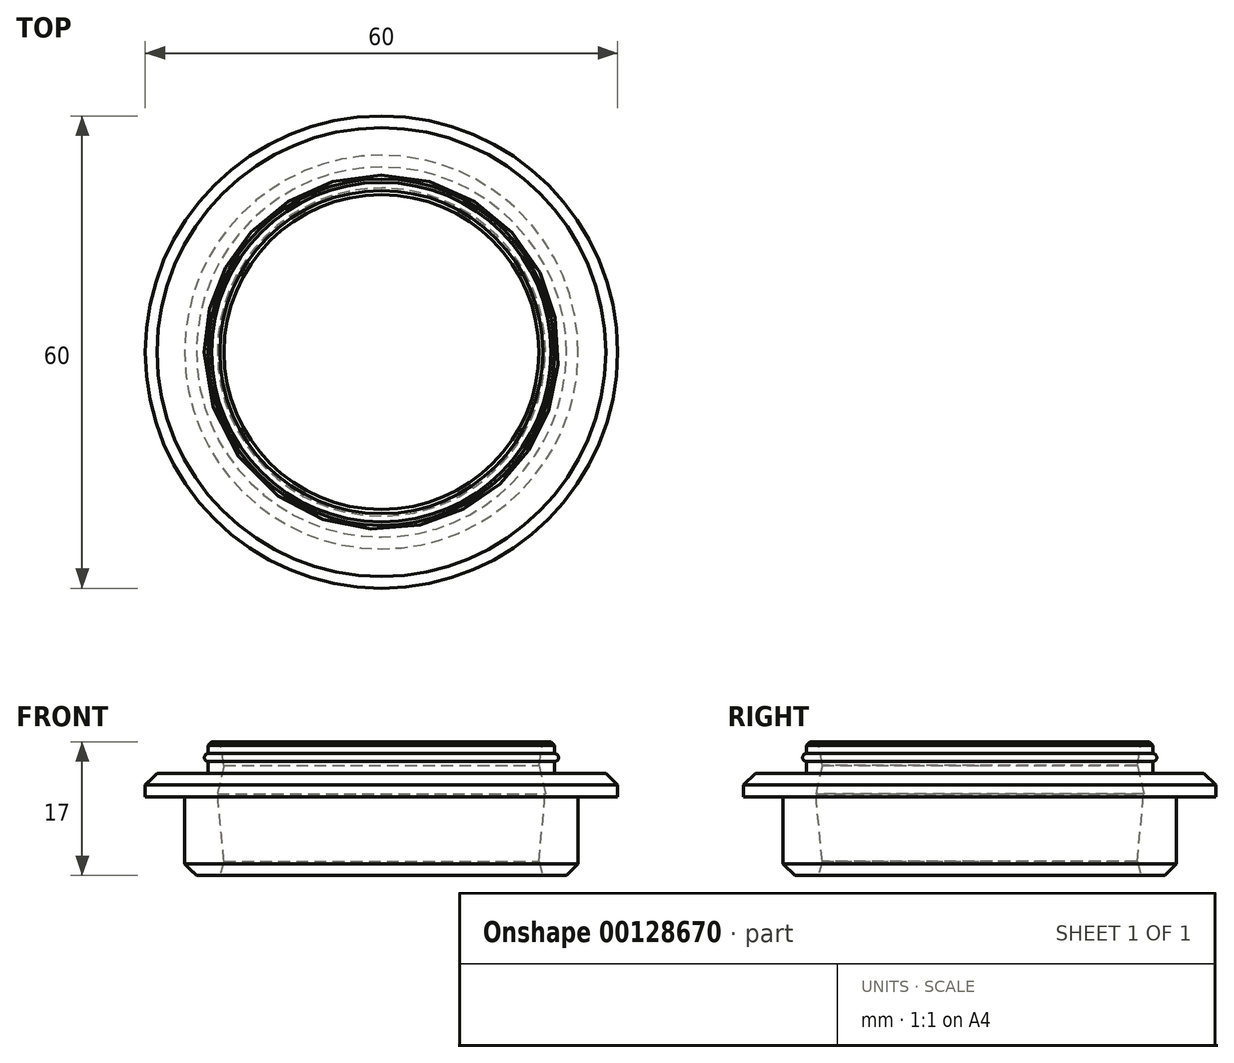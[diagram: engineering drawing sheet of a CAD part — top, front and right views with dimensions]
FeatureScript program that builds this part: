
annotation { "Feature Type Name" : "Feature", "Feature Type Description" : "" }
export const myFeature = defineFeature(function(context is Context, id is Id, definition is map)
    precondition{}
    {
        {
            var Q0;
            Q0=qCreatedBy(makeId("Front.planeOp"),FACE);
            var sketch = newSketch(context, id + "F0", { "sketchPlane" : qUnion([Q0])});
            skLineSegment(sketch, "E0", {"start": v(0, 0) * mm, "end": v(0, 42.45) * mm, "construction": true});
            skLineSegment(sketch, "E1.bottom", {"start": v(-20.54, 0) * mm, "end": v(-23.5, 0) * mm});
            skLineSegment(sketch, "E1.right", {"start": v(-25, 1.5) * mm, "end": v(-25, 10) * mm});
            skLineSegment(sketch, "E2", {"start": v(-25, 10) * mm, "end": v(-30, 10) * mm});
            skLineSegment(sketch, "E3", {"start": v(-30, 10) * mm, "end": v(-30, 11.5) * mm});
            skLineSegment(sketch, "E4", {"start": v(-28.5, 13) * mm, "end": v(-22, 13) * mm});
            skLineSegment(sketch, "E5", {"start": v(-22, 13) * mm, "end": v(-22, 14.5) * mm});
            skLineSegment(sketch, "E6", {"start": v(-21.56, 17) * mm, "end": v(-20.52, 17) * mm});
            skArc(sketch, "E7", {"start": v(-22, 15.5) * mm, "mid": v(-22.5, 15) * mm, "end": v(-22, 14.5) * mm});
            skLineSegment(sketch, "E8.trimOffspring", {"start": v(-22, 15.5) * mm, "end": v(-22, 16.56) * mm});
            skLineSegment(sketch, "E9", {"start": v(-20.54, 0) * mm, "end": v(-20, 1.78) * mm});
            skLineSegment(sketch, "E10", {"start": v(-20, 1.78) * mm, "end": v(-20.83, 10.4) * mm});
            skLineSegment(sketch, "E11", {"start": v(-20.83, 10.4) * mm, "end": v(-20, 14) * mm});
            skLineSegment(sketch, "E12", {"start": v(-20, 14) * mm, "end": v(-20.52, 17) * mm});
            skPoint(sketch, "E13.start.orphan", {"position": v(-20, 17) * mm});
            skPoint(sketch, "E14.orphan", {"position": v(-20, 0) * mm});
            skLineSegment(sketch, "E15", {"start": v(-30, 11.5) * mm, "end": v(-28.5, 13) * mm});
            skPoint(sketch, "E16.orphan", {"position": v(-30, 13) * mm});
            skLineSegment(sketch, "E17", {"start": v(-22, 16.56) * mm, "end": v(-21.56, 17) * mm});
            skPoint(sketch, "E18.orphan", {"position": v(-22, 17) * mm});
            skLineSegment(sketch, "E19", {"start": v(-23.5, 0) * mm, "end": v(-25, 1.5) * mm});
            skSolve(sketch);
        }
        {
            var Q0;
            Q0 = qSketchRegion(id + "F0", true);
            var Q1;
            Q1=sQuery(id+"F0.wireOp",EDGE,"E0");
            revolve(context, id + "F1", {"entities" : qUnion([Q0]), "axis" : qUnion([Q1]), "revolveType" : RevolveType.FULL});
        }
    });
